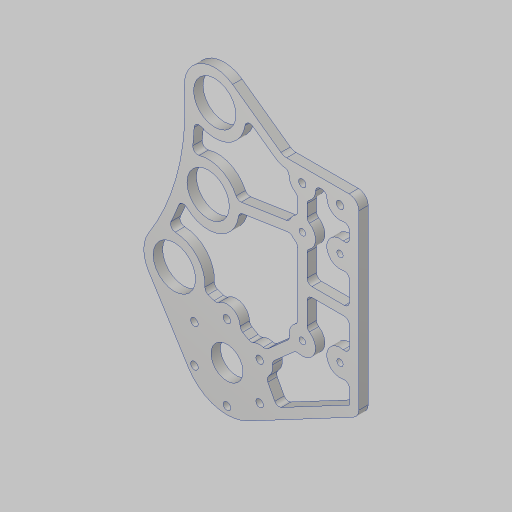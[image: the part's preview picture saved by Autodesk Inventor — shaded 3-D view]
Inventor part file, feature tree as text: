
AUTODESK INVENTOR PART (.ipt)
format: ipt  version: 2023.5 (Build 275446000, 446)  size: 432,128 bytes
history: native  units: in
note: dims shown in document units (in); Inventor stores cm internally (conversion verified against a paired STEP export)
features: sketch x4, hole x3, extrude x2, fillet x2, projected_geometry x2
ambient origin geometry x8: Origin, YZ Plane, XZ Plane, XY Plane, X Axis, Y Axis, Z Axis, Center Point
bodies: Solid1 (feature_tree)
feature tree (13):
  sketch  "Sketch1"  dims[d0=2.0in d1=15.0in]
  sketch  "Sketch2"  dims[d2=0.875in d3=17.0in]
  extrude  "Extrusion1"  Depth=2.0in
  hole  "Hole1"  [1 undecoded]
  hole  "Hole2"  [1 undecoded]
  fillet  "Fillet1"  Radius=1.0in
  hole  "Hole3"  [1 undecoded]
  extrude  "Extrusion2"  Depth=0.25in
  fillet  "Fillet2"  Radius=3.6in
  sketch  "Sketch3"  dims[d4=2.0in d5=17.0in d6=1.0in]
  projected_geometry  "Projected Loop1"
  sketch  "Sketch4"  dims[d7=0.2405in d8=2.4in d9=0.5in d10=3.6in d11=1.5in d12=1.5in d13=0.9in d14=3.7in d15=1.0in d16=3.4in d17=3.0in d20=2.0in d22=1.125in d23=4.297in d24=0.25in d25=2.0in d26=2.3622in d28=360.0deg d30=7.0in d31=2.0in d32=0.201in d33=1.0in d34=1.5in d35=1.0in d36=0.201in d37=1.0in d38=1.0in d39=2.5in d40=0.25in d41=0.0in d42=0.85in d43=0.201in d44=0.75in d45=0.385in d46=0.25in d47=0.5635in d48=1.0in d49=0.8108in d50=0.375in d51=0.171in d52=0.432in d53=0.385in d54=0.25in d55=0.5635in d56=1.0in d57=0.8108in d58=0.26in d59=1.825in d60=0.25in d61=0.25in d62=0.25in d63=1.0in d64=0.125in d65=0.125in d66=0.125in d67=0.125in d68=0.125in d69=0.125in d70=1.0in d71=0.0in d72=0.13in d74=1.75in d75=0.875in d76=0.156in d77=0.38in d78=0.375in d79=0.25in d80=0.5635in d81=1.0in d82=0.8108in d83=0.125in d84=0.125in]
  projected_geometry  "Projected Loop2"
note: 3 required parameter values undecoded (feature->parameter linkage not recoverable at this tier; creation-order binding heuristic only, values carry confidence <= 0.55)
